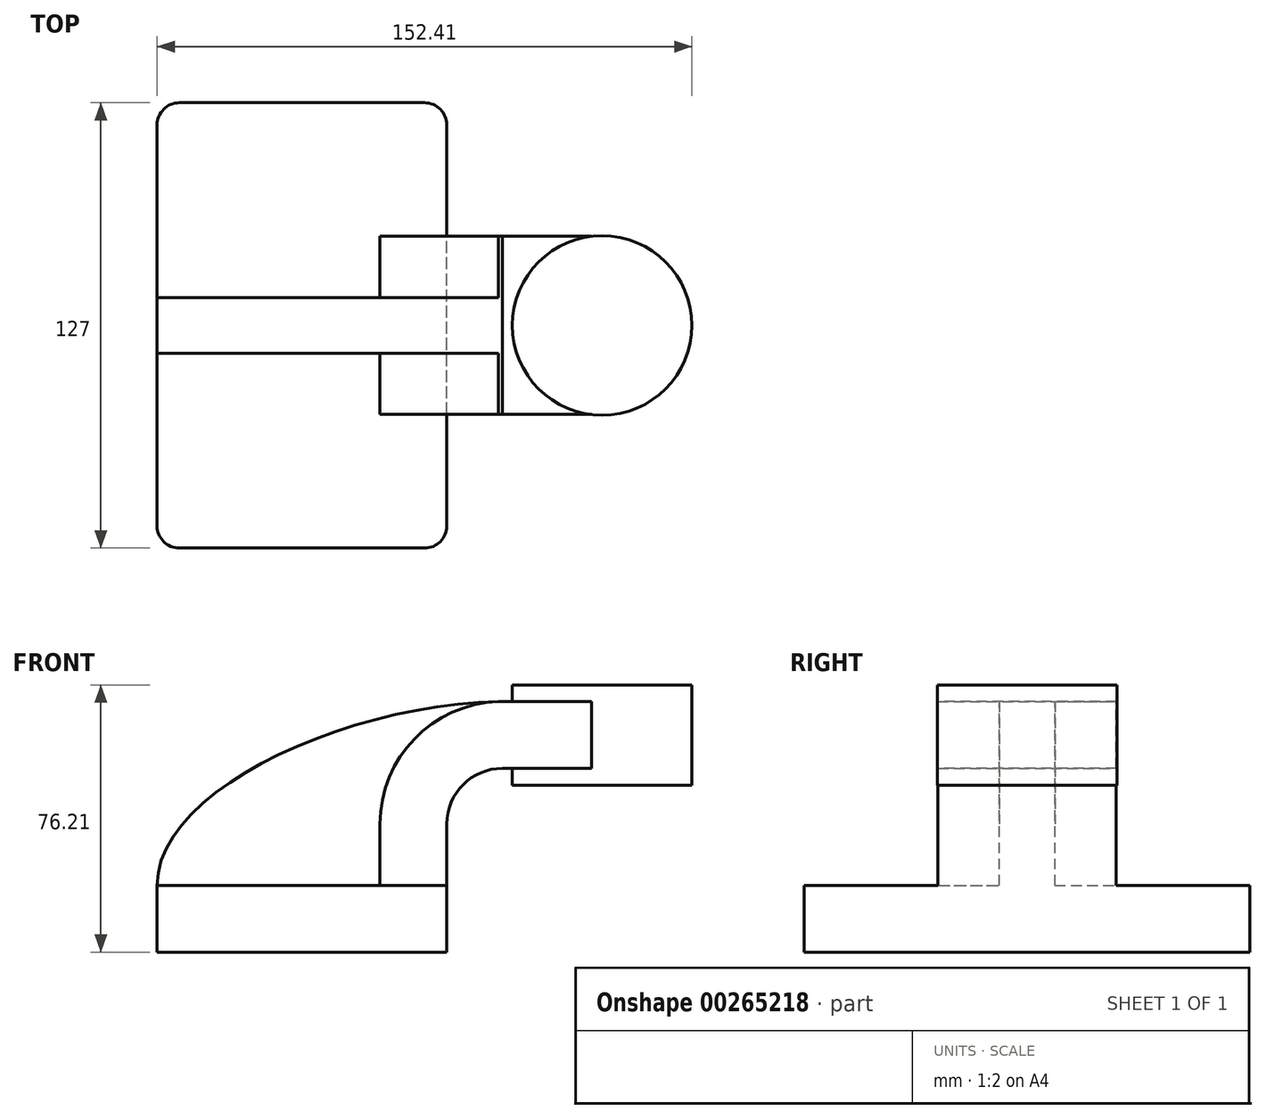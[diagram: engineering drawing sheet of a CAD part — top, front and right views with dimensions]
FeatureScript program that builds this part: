
annotation { "Feature Type Name" : "Feature", "Feature Type Description" : "" }
export const myFeature = defineFeature(function(context is Context, id is Id, definition is map)
    precondition{}
    {
        {
            var Q0;
            Q0=qCreatedBy(makeId("Front.planeOp"),FACE);
            var sketch = newSketch(context, id + "F0", { "sketchPlane" : qUnion([Q0])});
            skLineSegment(sketch, "E0.bottom", {"start": v(-41.28, 9.52) * mm, "end": v(41.27, 9.53) * mm});
            skLineSegment(sketch, "E0.top", {"start": v(-41.28, -9.53) * mm, "end": v(41.28, -9.53) * mm});
            skLineSegment(sketch, "E0.left", {"start": v(-41.28, 9.52) * mm, "end": v(-41.27, -9.53) * mm});
            skLineSegment(sketch, "E0.right", {"start": v(41.28, 9.53) * mm, "end": v(41.28, -9.52) * mm});
            skPoint(sketch, "E0.middle", {"position": v(0, 0) * mm});
            skLineSegment(sketch, "E1.bottom", {"start": v(60.33, 38.1) * mm, "end": v(111.13, 38.1) * mm});
            skLineSegment(sketch, "E1.top", {"start": v(60.33, 66.67) * mm, "end": v(111.13, 66.67) * mm});
            skLineSegment(sketch, "E1.left", {"start": v(60.33, 38.1) * mm, "end": v(60.33, 66.67) * mm});
            skLineSegment(sketch, "E1.right", {"start": v(111.13, 38.1) * mm, "end": v(111.13, 66.67) * mm});
            skPoint(sketch, "E1.middle", {"position": v(85.73, 52.39) * mm});
            skLineSegment(sketch, "E2", {"start": v(41.27, 9.53) * mm, "end": v(41.27, 27) * mm});
            skArc(sketch, "E3", {"start": v(41.27, 27) * mm, "mid": v(45.92, 38.23) * mm, "end": v(57.15, 42.88) * mm});
            skLineSegment(sketch, "E4", {"start": v(57.15, 42.88) * mm, "end": v(85.54, 42.88) * mm});
            skLineSegment(sketch, "E5.0", {"start": v(57.15, 61.93) * mm, "end": v(85.54, 61.93) * mm});
            skArc(sketch, "E5.1", {"start": v(22.23, 27) * mm, "mid": v(32.45, 51.7) * mm, "end": v(57.15, 61.93) * mm});
            skLineSegment(sketch, "E5.2", {"start": v(22.22, 9.53) * mm, "end": v(22.22, 27) * mm});
            skFitSpline(sketch, "E6", {"points": [v(-41.28, 9.53) * mm, v(57.15, 61.93) * mm], "startDerivative": vector(0.03, 82.1) * mm, "endDerivative": vector(132.53, 1.55) * mm});
            skLineSegment(sketch, "E7", {"start": v(85.54, 66.67) * mm, "end": v(85.54, 38.1) * mm});
            skSolve(sketch);
        }
        {
            var Q0;
            Q0=makeQuery(id+"F0.imprint","IMPRINT",FACE,{"disambiguationData":[TD([[makeQuery(id+"F0.imprint","IMPRINT",EDGE,{"derivedFrom":sQuery(id+"F0.wireOp",EDGE,"E0.top")}),1.0]])]});
            extrude(context, id + "F1", {"entities" : qUnion([Q0]), "endBound" : BoundingType.SYMMETRIC, "depth" : 127 * mm});
        }
        {
            var Q0;
            {var subQ5=sQuery(id+"F0.wireOp",EDGE,"KfTRVusd-Lg7a-br6O-sqEO-IOsCI29nXDK8");Q0=makeQuery(id+"F0.imprint","IMPRINT",FACE,{"disambiguationData":[TD([[makeQuery(id+"F0.imprint","IMPRINT",EDGE,{"derivedFrom":subQ5}),1.0]])]});}
            var Q1;
            {var subQ1=sQuery(id+"F0.wireOp",EDGE,"E2");Q1=makeQuery(id+"F0.imprint","IMPRINT",FACE,{"disambiguationData":[TD([[makeQuery(id+"F0.imprint","IMPRINT",EDGE,{"derivedFrom":subQ1}),1.0]])]});}
            var Q2;
            {var subQ0=sQuery(id+"F0.wireOp",EDGE,"E4");var subQ1=sQuery(id+"F0.wireOp",EDGE,"E1.left");var subQ2=makeQuery(id+"F0.imprint","INTERSECT",VERTEX,{"derivedFrom":[subQ1,subQ0]});Q2=makeQuery(id+"F0.imprint","IMPRINT",FACE,{"disambiguationData":[TD([[makeQuery(id+"F0.imprint","IMPRINT",EDGE,{"disambiguationData":[TD([[subQ2,-1.0]])],"derivedFrom":subQ1}),-1.0]])]});}
            extrude(context, id + "F2", {"entities" : qUnion([Q0, Q1, Q2]), "operationType" : NewBodyOperationType.ADD, "endBound" : BoundingType.SYMMETRIC, "depth" : 50.8 * mm});
        }
        {
            var Q0;
            {var subQ3=sQuery(id+"F0.wireOp",EDGE,"E5.2");Q0=makeQuery(id+"F0.imprint","IMPRINT",FACE,{"disambiguationData":[TD([[makeQuery(id+"F0.imprint","IMPRINT",EDGE,{"derivedFrom":subQ3}),1.0]])]});}
            extrude(context, id + "F3", {"entities" : qUnion([Q0]), "operationType" : NewBodyOperationType.ADD, "endBound" : BoundingType.SYMMETRIC, "depth" : 15.88 * mm});
        }
        {
            var Q0;
            {var subQ0=sQuery(id+"F0.wireOp",EDGE,"E1.right");Q0=makeQuery(id+"F0.imprint","IMPRINT",FACE,{"disambiguationData":[TD([[makeQuery(id+"F0.imprint","IMPRINT",EDGE,{"derivedFrom":subQ0}),1.0]])]});}
            var Q1;
            Q1=sQuery(id+"F0.wireOp",EDGE,"E7");
            revolve(context, id + "F4", {"operationType" : NewBodyOperationType.ADD, "entities" : qUnion([Q0]), "axis" : qUnion([Q1]), "revolveType" : RevolveType.FULL});
        }
        {
            var Q0;
            Q0=makeQuery(id+"F1.opExtrude","CAP_EDGE",EDGE,{"disambiguationData":[OSD([sQuery(id+"F0.wireOp",EDGE,"E0.right")])],"isStart":false});
            var Q1;
            Q1=makeQuery(id+"F1.opExtrude","CAP_EDGE",EDGE,{"disambiguationData":[OSD([sQuery(id+"F0.wireOp",EDGE,"E0.left")])],"isStart":false});
            var Q2;
            Q2=makeQuery(id+"F1.opExtrude","CAP_EDGE",EDGE,{"disambiguationData":[OSD([sQuery(id+"F0.wireOp",EDGE,"E0.right")])],"isStart":true});
            var Q3;
            Q3=makeQuery(id+"F1.opExtrude","CAP_EDGE",EDGE,{"disambiguationData":[OSD([sQuery(id+"F0.wireOp",EDGE,"E0.left")])],"isStart":true});
            fillet(context, id + "F5", {"entities" : qUnion([Q0, Q1, Q2, Q3]), "radius" : 6.35 * mm, "tangentPropagation" : true, "allowEdgeOverflow" : false});
        }
    });
